# Revit family: Spot 2.4
name_source: partatom
category: Lighting Fixtures
revit_build: Autodesk Revit 2017 (Build: 20170419_0315(x64)
units: mm (PartAtom-declared; Revit-internal decimal feet)

## family parameters
Always vertical = No
Cut with Voids When Loaded = No
Light Source = No
OmniClass Number = 23.80.70.00
OmniClass Title = Lighting
Part Type = Normal
Room Calculation Point = Yes
Round Connector Dimension = Use Diameter
Shared = No
Work Plane-Based = No

## types (3) — shared parameters
Apparent Load Phase 1 = 8 W
Base = L&L_Stainless steel
Base bracket = Spot2.4_Base braket
Body = L&L_White
Bracket = L&L_Grey aluminium
CRI = 80
Code = CF2410000050SH Anthracite; CF2410000050SE White
Control system = -
Cutout dimensions = -
Delivered lumen output = 515 lm (3000K, 34°)
Description = Outdoor projectors
Energy efficiency class = A A+ A++
Features = -
Geometry = Spot2.4_mod
Height mm = 143 mm
IP = 66
LED Colour = 3000K (also available: 4000K - ref. URL Technical sheet)
Length mm = 95 mm  [stored 0.31168 ft]
Lens = L&L_Tempered extra-clear glass
Lumen output at source = 781 lm (3000K)
Manufacturer = L&L Luce&Light
Material = body in anticorodal aluminium, screen in serigraphed, transparent and tempered extra-clear glass
Model = Spot 2.4
Mounting = surface mounted (ceiling, wall, ground, spike)
No. and type of led = 1 power LED High Intensity, 3-step MacAdam, 50 000h L85 B10 (Ta 25°C)
Notes = -
Power = 8W
Power cables = includes 1,5 m neoprene cable H05RN-F 3x1,0 Ø7 mm
Power supply = 230Vac
Power supply unit = built-in
URL = https://www.lucelight.it
URL Accessories and power supply units = https://www.lucelight.it
URL Catalogue = https://www.lucelight.it
URL DXF = https://www.lucelight.it
URL Description = https://www.lucelight.it
URL General code = https://www.lucelight.it
URL IES Photometric file = https://www.lucelight.it
URL Image = https://www.lucelight.it
URL Technical sheet = https://www.lucelight.it
Vertical rotation max = 240.00°
Voltage = 230 V
Weight kg = 0.70 kg
Width mm = 60 mm  [stored 0.19685 ft]
Wiring = -

## per-type parameters (varying)
| type | Light Source | Optics |
| Spot 2.4_L 60° (3000K 8W 230Vac) | Light Source : L60° | 60° |
| Spot 2.4_M 34° (3000K 8W 230Vac) | Light Source : M34° | 34° |
| Spot 2.4_S 20° (3000K 8W 230Vac) | Light Source : S20° | 20° |

note: [stored X ft] marks values corroborated as IEEE doubles in the binary element streams (Revit-internal decimal feet)

## geometry (parser evidence)
native form markers: Blend x2, Sweep x14
no freeform markers — native parametric forms only
